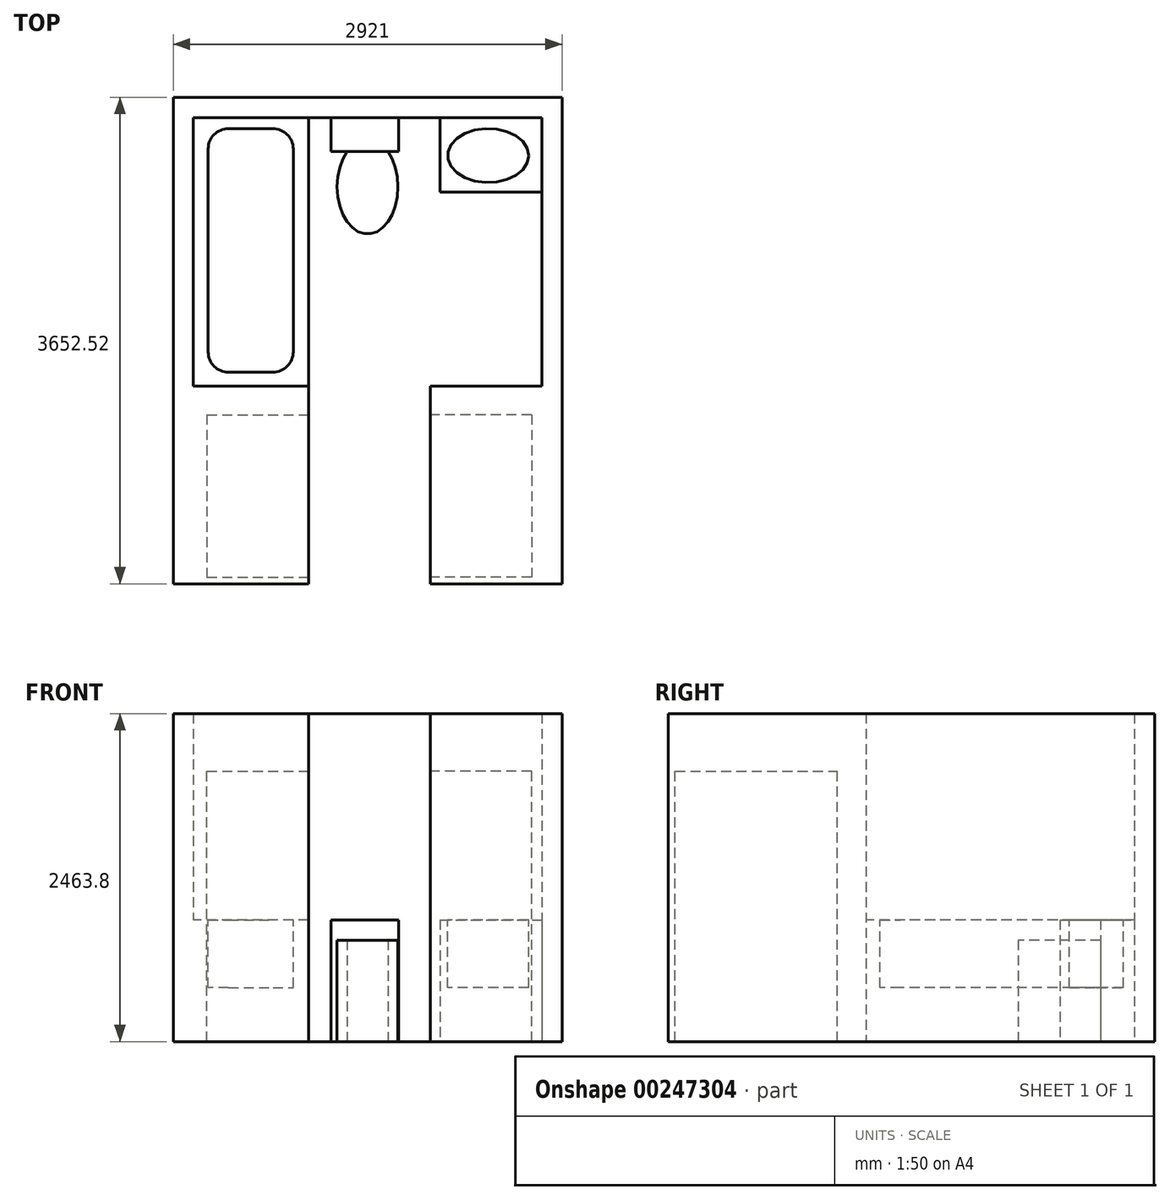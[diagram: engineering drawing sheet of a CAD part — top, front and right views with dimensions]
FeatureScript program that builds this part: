
annotation { "Feature Type Name" : "Feature", "Feature Type Description" : "" }
export const myFeature = defineFeature(function(context is Context, id is Id, definition is map)
    precondition{}
    {
        {
            var Q0;
            Q0=qCreatedBy(makeId("Top.planeOp"),FACE);
            var sketch = newSketch(context, id + "F0", { "sketchPlane" : qUnion([Q0])});
            skLineSegment(sketch, "E0.bottom", {"start": v(-1198.42, 0) * mm, "end": v(-334.82, 0) * mm});
            skLineSegment(sketch, "E0.top", {"start": v(-1350.82, -1333.5) * mm, "end": v(-334.82, -1333.5) * mm});
            skLineSegment(sketch, "E0.left", {"start": v(-1350.82, 0) * mm, "end": v(-1350.82, -1333.5) * mm});
            skLineSegment(sketch, "E0.right", {"start": v(-334.82, 0) * mm, "end": v(-334.82, -1333.5) * mm});
            skLineSegment(sketch, "E1.bottom", {"start": v(579.58, 0) * mm, "end": v(1417.78, 0) * mm});
            skLineSegment(sketch, "E1.top", {"start": v(579.58, -1333.5) * mm, "end": v(1570.18, -1333.5) * mm});
            skLineSegment(sketch, "E1.left", {"start": v(579.58, 0) * mm, "end": v(579.58, -1333.5) * mm});
            skLineSegment(sketch, "E1.right", {"start": v(1570.18, 0) * mm, "end": v(1570.18, -1333.5) * mm});
            skLineSegment(sketch, "E2", {"start": v(-1350.82, 0) * mm, "end": v(-1350.82, 2319.02) * mm});
            skLineSegment(sketch, "E3", {"start": v(-1350.82, 2319.02) * mm, "end": v(1570.18, 2319.02) * mm});
            skLineSegment(sketch, "E4", {"start": v(1570.18, 0) * mm, "end": v(1570.18, 2319.02) * mm});
            skLineSegment(sketch, "E5.0", {"start": v(-1198.42, 0) * mm, "end": v(-1198.42, 2166.62) * mm});
            skLineSegment(sketch, "E6.0", {"start": v(-1198.42, 2166.62) * mm, "end": v(1417.78, 2166.62) * mm});
            skLineSegment(sketch, "E7.0", {"start": v(1417.78, 0) * mm, "end": v(1417.78, 2166.62) * mm});
            skSolve(sketch);
        }
        {
            var Q0;
            Q0 = qSketchRegion(id + "F0", true);
            extrude(context, id + "F1", {"entities" : qUnion([Q0]), "depth" : 2463.8 * mm});
        }
        {
            var Q0;
            Q0=makeQuery(id+"F1.opExtrude","SWEPT_FACE",FACE,{"disambiguationData":[OSD([sQuery(id+"F0.wireOp",EDGE,"E0.right")])]});
            var sketch = newSketch(context, id + "F2", { "sketchPlane" : qUnion([Q0])});
            skLineSegment(sketch, "E8.bottom", {"start": v(-1282.7, 0) * mm, "end": v(-63.5, 0) * mm});
            skLineSegment(sketch, "E8.top", {"start": v(-1282.7, 2032) * mm, "end": v(-63.5, 2032) * mm});
            skLineSegment(sketch, "E8.left", {"start": v(-1282.7, 0) * mm, "end": v(-1282.7, 2032) * mm});
            skLineSegment(sketch, "E8.right", {"start": v(-63.5, 0) * mm, "end": v(-63.5, 2032) * mm});
            skSolve(sketch);
        }
        {
            var Q0;
            Q0=makeQuery(id+"F2.imprint","IMPRINT",FACE,{"disambiguationData":[TD([[makeQuery(id+"F2.imprint","IMPRINT",EDGE,{"derivedFrom":sQuery(id+"F2.wireOp",EDGE,"E8.bottom")}),-1.0]])]});
            extrude(context, id + "F3", {"entities" : qUnion([Q0]), "operationType" : NewBodyOperationType.REMOVE, "oppositeDirection" : true, "depth" : 762 * mm});
        }
        {
            var Q0;
            Q0=makeQuery(id+"F1.opExtrude","SWEPT_FACE",FACE,{"disambiguationData":[OSD([sQuery(id+"F0.wireOp",EDGE,"E1.left")])]});
            var sketch = newSketch(context, id + "F4", { "sketchPlane" : qUnion([Q0])});
            skLineSegment(sketch, "E9.bottom", {"start": v(63.5, 0) * mm, "end": v(1282.7, 0) * mm});
            skLineSegment(sketch, "E9.top", {"start": v(63.5, 2032) * mm, "end": v(1282.7, 2032) * mm});
            skLineSegment(sketch, "E9.left", {"start": v(63.5, 0) * mm, "end": v(63.5, 2032) * mm});
            skLineSegment(sketch, "E9.right", {"start": v(1282.7, 0) * mm, "end": v(1282.7, 2032) * mm});
            skSolve(sketch);
        }
        {
            var Q0;
            Q0=makeQuery(id+"F4.imprint","IMPRINT",FACE,{"disambiguationData":[TD([[makeQuery(id+"F4.imprint","IMPRINT",EDGE,{"derivedFrom":sQuery(id+"F4.wireOp",EDGE,"E9.bottom")}),1.0]])]});
            extrude(context, id + "F5", {"entities" : qUnion([Q0]), "operationType" : NewBodyOperationType.REMOVE, "oppositeDirection" : true, "depth" : 762 * mm});
        }
        {
            var Q0;
            Q0=makeQuery(id+"F1.opExtrude","CAP_FACE",FACE,{"disambiguationData":[OSD([sQuery(id+"F0.wireOp",EDGE,"E0.bottom"),sQuery(id+"F0.wireOp",EDGE,"E0.top"),sQuery(id+"F0.wireOp",EDGE,"E0.left"),sQuery(id+"F0.wireOp",EDGE,"E0.right"),sQuery(id+"F0.wireOp",EDGE,"E1.bottom"),sQuery(id+"F0.wireOp",EDGE,"E1.top"),sQuery(id+"F0.wireOp",EDGE,"E1.left"),sQuery(id+"F0.wireOp",EDGE,"E1.right"),sQuery(id+"F0.wireOp",EDGE,"E2"),sQuery(id+"F0.wireOp",EDGE,"E3"),sQuery(id+"F0.wireOp",EDGE,"E4"),sQuery(id+"F0.wireOp",EDGE,"E5.0"),sQuery(id+"F0.wireOp",EDGE,"E6.0"),sQuery(id+"F0.wireOp",EDGE,"E7.0")])],"isStart":true});
            var sketch = newSketch(context, id + "F6", { "sketchPlane" : qUnion([Q0])});
            skLineSegment(sketch, "E10.bottom", {"start": v(1417.78, -2166.62) * mm, "end": v(655.78, -2166.62) * mm});
            skLineSegment(sketch, "E10.top", {"start": v(1417.78, -1607.82) * mm, "end": v(655.78, -1607.82) * mm});
            skLineSegment(sketch, "E10.left", {"start": v(1417.78, -2166.62) * mm, "end": v(1417.78, -1607.82) * mm});
            skLineSegment(sketch, "E10.right", {"start": v(655.78, -2166.62) * mm, "end": v(655.78, -1607.82) * mm});
            skLineSegment(sketch, "E11.bottom", {"start": v(-1198.42, -2166.62) * mm, "end": v(-334.82, -2166.62) * mm});
            skLineSegment(sketch, "E11.top", {"start": v(-1198.42, 0) * mm, "end": v(-334.82, 0) * mm});
            skLineSegment(sketch, "E11.left", {"start": v(-1198.42, -2166.62) * mm, "end": v(-1198.42, 0) * mm});
            skLineSegment(sketch, "E11.right", {"start": v(-334.82, -2166.62) * mm, "end": v(-334.82, 0) * mm});
            skLineSegment(sketch, "E12.bottom", {"start": v(-165.39, -2166.62) * mm, "end": v(342.61, -2166.62) * mm});
            skLineSegment(sketch, "E12.top", {"start": v(-165.39, -1912.62) * mm, "end": v(342.61, -1912.62) * mm});
            skLineSegment(sketch, "E12.left", {"start": v(-165.39, -2166.62) * mm, "end": v(-165.39, -1912.62) * mm});
            skLineSegment(sketch, "E12.right", {"start": v(342.61, -2166.62) * mm, "end": v(342.61, -1912.62) * mm});
            skSolve(sketch);
        }
        {
            var Q0;
            Q0 = qSketchRegion(id + "F6", true);
            extrude(context, id + "F7", {"entities" : qUnion([Q0]), "operationType" : NewBodyOperationType.ADD, "oppositeDirection" : true, "depth" : 914.4 * mm});
        }
        {
            var Q0;
            Q0=makeQuery(id+"F7.boolean.opBoolean","MERGE",FACE,{"derivedFrom":[makeQuery(id+"F1.opExtrude","CAP_FACE",FACE,{"disambiguationData":[OSD([sQuery(id+"F0.wireOp",EDGE,"E0.bottom"),sQuery(id+"F0.wireOp",EDGE,"E0.top"),sQuery(id+"F0.wireOp",EDGE,"E0.left"),sQuery(id+"F0.wireOp",EDGE,"E0.right"),sQuery(id+"F0.wireOp",EDGE,"E1.bottom"),sQuery(id+"F0.wireOp",EDGE,"E1.top"),sQuery(id+"F0.wireOp",EDGE,"E1.left"),sQuery(id+"F0.wireOp",EDGE,"E1.right"),sQuery(id+"F0.wireOp",EDGE,"E2"),sQuery(id+"F0.wireOp",EDGE,"E3"),sQuery(id+"F0.wireOp",EDGE,"E4"),sQuery(id+"F0.wireOp",EDGE,"E5.0"),sQuery(id+"F0.wireOp",EDGE,"E6.0"),sQuery(id+"F0.wireOp",EDGE,"E7.0")])],"isStart":true}),makeQuery(id+"F7.opExtrude","CAP_FACE",FACE,{"disambiguationData":[OSD([sQuery(id+"F6.wireOp",EDGE,"E10.bottom"),sQuery(id+"F6.wireOp",EDGE,"E10.top"),sQuery(id+"F6.wireOp",EDGE,"E10.left"),sQuery(id+"F6.wireOp",EDGE,"E10.right")])],"isStart":true}),makeQuery(id+"F7.opExtrude","CAP_FACE",FACE,{"disambiguationData":[OSD([sQuery(id+"F6.wireOp",EDGE,"E11.bottom"),sQuery(id+"F6.wireOp",EDGE,"E11.top"),sQuery(id+"F6.wireOp",EDGE,"E11.left"),sQuery(id+"F6.wireOp",EDGE,"E11.right")])],"isStart":true}),makeQuery(id+"F7.opExtrude","CAP_FACE",FACE,{"disambiguationData":[OSD([sQuery(id+"F6.wireOp",EDGE,"E12.bottom"),sQuery(id+"F6.wireOp",EDGE,"E12.top"),sQuery(id+"F6.wireOp",EDGE,"E12.left"),sQuery(id+"F6.wireOp",EDGE,"E12.right")])],"isStart":true})]});
            var sketch = newSketch(context, id + "F8", { "sketchPlane" : qUnion([Q0])});
            skEllipse(sketch, "E13", {"center": v(109.68, -1649.28) * mm, "majorRadius": 355.6 * mm, "minorRadius": 228.6 * mm, "majorAxis": v(0, 1)});
            skSolve(sketch);
        }
        {
            var Q0;
            Q0 = qSketchRegion(id + "F8", true);
            extrude(context, id + "F9", {"entities" : qUnion([Q0]), "operationType" : NewBodyOperationType.ADD, "oppositeDirection" : true, "depth" : 762 * mm});
        }
        {
            var Q0;
            Q0=makeQuery(id+"F7.opExtrude","CAP_FACE",FACE,{"disambiguationData":[OSD([sQuery(id+"F6.wireOp",EDGE,"E11.bottom"),sQuery(id+"F6.wireOp",EDGE,"E11.top"),sQuery(id+"F6.wireOp",EDGE,"E11.left"),sQuery(id+"F6.wireOp",EDGE,"E11.right")])],"isStart":false});
            var sketch = newSketch(context, id + "F10", { "sketchPlane" : qUnion([Q0])});
            skLineSegment(sketch, "E14.bottom", {"start": v(-935.5, 2085.16) * mm, "end": v(-601.52, 2085.16) * mm});
            skLineSegment(sketch, "E14.top", {"start": v(-935.5, 256.36) * mm, "end": v(-601.52, 256.36) * mm});
            skLineSegment(sketch, "E14.left", {"start": v(-1087.9, 1932.76) * mm, "end": v(-1087.9, 408.76) * mm});
            skLineSegment(sketch, "E15", {"start": v(-449.12, 1932.76) * mm, "end": v(-449.12, 408.76) * mm});
            skPoint(sketch, "E16.visualSharp", {"position": v(-1087.9, 2085.16) * mm});
            skArc(sketch, "E16.filletArc", {"start": v(-935.5, 2085.16) * mm, "mid": v(-1043.26, 2040.52) * mm, "end": v(-1087.9, 1932.76) * mm});
            skPoint(sketch, "E17.visualSharp", {"position": v(-449.12, 2085.16) * mm});
            skArc(sketch, "E17.filletArc", {"start": v(-449.12, 1932.76) * mm, "mid": v(-493.76, 2040.52) * mm, "end": v(-601.52, 2085.16) * mm});
            skPoint(sketch, "E18.visualSharp", {"position": v(-1087.9, 256.36) * mm});
            skArc(sketch, "E18.filletArc", {"start": v(-1087.9, 408.76) * mm, "mid": v(-1043.26, 301) * mm, "end": v(-935.5, 256.36) * mm});
            skPoint(sketch, "E19.visualSharp", {"position": v(-449.12, 256.36) * mm});
            skArc(sketch, "E19.filletArc", {"start": v(-601.52, 256.36) * mm, "mid": v(-493.76, 301) * mm, "end": v(-449.12, 408.76) * mm});
            skEllipse(sketch, "E20", {"center": v(1016.17, 1882.7) * mm, "majorRadius": 304.8 * mm, "minorRadius": 203.2 * mm, "majorAxis": v(1, 0)});
            skSolve(sketch);
        }
        {
            var Q0;
            Q0 = qSketchRegion(id + "F10", true);
            extrude(context, id + "F11", {"entities" : qUnion([Q0]), "operationType" : NewBodyOperationType.REMOVE, "oppositeDirection" : true, "depth" : 508 * mm});
        }
        {
            var Q0;
            Q0=makeQuery(id+"F9.boolean.opBoolean","MERGE",FACE,{"derivedFrom":[makeQuery(id+"F7.boolean.opBoolean","MERGE",FACE,{"derivedFrom":[makeQuery(id+"F1.opExtrude","CAP_FACE",FACE,{"disambiguationData":[OSD([sQuery(id+"F0.wireOp",EDGE,"E0.bottom"),sQuery(id+"F0.wireOp",EDGE,"E0.top"),sQuery(id+"F0.wireOp",EDGE,"E0.left"),sQuery(id+"F0.wireOp",EDGE,"E0.right"),sQuery(id+"F0.wireOp",EDGE,"E1.bottom"),sQuery(id+"F0.wireOp",EDGE,"E1.top"),sQuery(id+"F0.wireOp",EDGE,"E1.left"),sQuery(id+"F0.wireOp",EDGE,"E1.right"),sQuery(id+"F0.wireOp",EDGE,"E2"),sQuery(id+"F0.wireOp",EDGE,"E3"),sQuery(id+"F0.wireOp",EDGE,"E4"),sQuery(id+"F0.wireOp",EDGE,"E5.0"),sQuery(id+"F0.wireOp",EDGE,"E6.0"),sQuery(id+"F0.wireOp",EDGE,"E7.0")])],"isStart":true}),makeQuery(id+"F7.opExtrude","CAP_FACE",FACE,{"disambiguationData":[OSD([sQuery(id+"F6.wireOp",EDGE,"E10.bottom"),sQuery(id+"F6.wireOp",EDGE,"E10.top"),sQuery(id+"F6.wireOp",EDGE,"E10.left"),sQuery(id+"F6.wireOp",EDGE,"E10.right")])],"isStart":true}),makeQuery(id+"F7.opExtrude","CAP_FACE",FACE,{"disambiguationData":[OSD([sQuery(id+"F6.wireOp",EDGE,"E11.bottom"),sQuery(id+"F6.wireOp",EDGE,"E11.top"),sQuery(id+"F6.wireOp",EDGE,"E11.left"),sQuery(id+"F6.wireOp",EDGE,"E11.right")])],"isStart":true}),makeQuery(id+"F7.opExtrude","CAP_FACE",FACE,{"disambiguationData":[OSD([sQuery(id+"F6.wireOp",EDGE,"E12.bottom"),sQuery(id+"F6.wireOp",EDGE,"E12.top"),sQuery(id+"F6.wireOp",EDGE,"E12.left"),sQuery(id+"F6.wireOp",EDGE,"E12.right")])],"isStart":true})]}),makeQuery(id+"F9.opExtrude","CAP_FACE",FACE,{"disambiguationData":[OSD([sQuery(id+"F8.wireOp",EDGE,"E13")])],"isStart":true})]});
            var sketch = newSketch(context, id + "F12", { "sketchPlane" : qUnion([Q0])});
            skLineSegment(sketch, "E21.bottom", {"start": v(579.58, 0) * mm, "end": v(1417.78, 0) * mm});
            skLineSegment(sketch, "E21.top", {"start": v(579.58, -152.4) * mm, "end": v(1417.78, -152.4) * mm});
            skLineSegment(sketch, "E21.left", {"start": v(579.58, 0) * mm, "end": v(579.58, -152.4) * mm});
            skLineSegment(sketch, "E21.right", {"start": v(1417.78, 0) * mm, "end": v(1417.78, -152.4) * mm});
            skLineSegment(sketch, "E22.bottom", {"start": v(-334.82, 0) * mm, "end": v(-1198.42, 0) * mm});
            skLineSegment(sketch, "E22.top", {"start": v(-334.82, -152.4) * mm, "end": v(-1198.42, -152.4) * mm});
            skLineSegment(sketch, "E22.left", {"start": v(-334.82, 0) * mm, "end": v(-334.82, -152.4) * mm});
            skLineSegment(sketch, "E22.right", {"start": v(-1198.42, 0) * mm, "end": v(-1198.42, -152.4) * mm});
            skSolve(sketch);
        }
        {
            var Q0;
            Q0 = qSketchRegion(id + "F12", true);
            var Q1;
            Q1=makeQuery(id+"F1.opExtrude","CAP_FACE",FACE,{"disambiguationData":[OSD([sQuery(id+"F0.wireOp",EDGE,"E0.bottom"),sQuery(id+"F0.wireOp",EDGE,"E0.top"),sQuery(id+"F0.wireOp",EDGE,"E0.left"),sQuery(id+"F0.wireOp",EDGE,"E0.right"),sQuery(id+"F0.wireOp",EDGE,"E1.bottom"),sQuery(id+"F0.wireOp",EDGE,"E1.top"),sQuery(id+"F0.wireOp",EDGE,"E1.left"),sQuery(id+"F0.wireOp",EDGE,"E1.right"),sQuery(id+"F0.wireOp",EDGE,"E2"),sQuery(id+"F0.wireOp",EDGE,"E3"),sQuery(id+"F0.wireOp",EDGE,"E4"),sQuery(id+"F0.wireOp",EDGE,"E5.0"),sQuery(id+"F0.wireOp",EDGE,"E6.0"),sQuery(id+"F0.wireOp",EDGE,"E7.0")])],"isStart":false});
            extrude(context, id + "F13", {"entities" : qUnion([Q0]), "operationType" : NewBodyOperationType.ADD, "endBound" : BoundingType.UP_TO_SURFACE, "oppositeDirection" : true, "endBoundEntityFace" : qUnion([Q1]), "depth" : 25.4 * mm});
        }
    });
